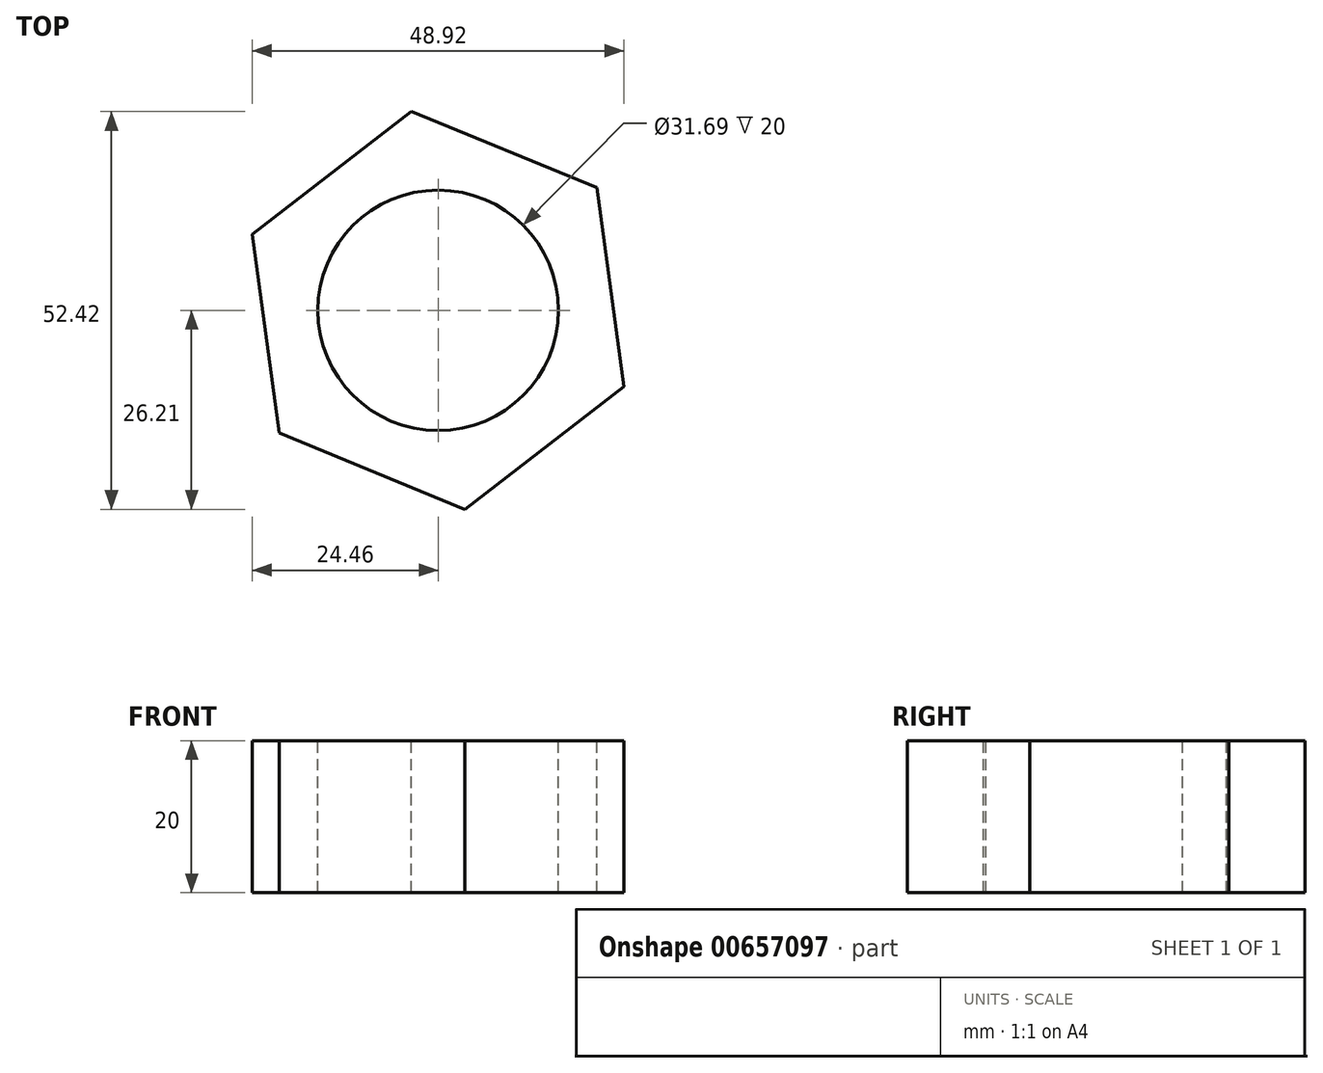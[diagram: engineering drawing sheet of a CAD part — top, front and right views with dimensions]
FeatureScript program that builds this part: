
annotation { "Feature Type Name" : "Feature", "Feature Type Description" : "" }
export const myFeature = defineFeature(function(context is Context, id is Id, definition is map)
    precondition{}
    {
        {
            var Q0;
            Q0=qCreatedBy(makeId("Top.planeOp"),FACE);
            var sketch = newSketch(context, id + "F0", { "sketchPlane" : qUnion([Q0])});
            skCircle(sketch, "E0.cCircle", {"center": v(0, 0) * mm, "radius": 22.9 * mm, "construction": true});
            skLineSegment(sketch, "E0.0", {"start": v(-3.52, 26.21) * mm, "end": v(20.94, 16.16) * mm});
            skLineSegment(sketch, "E0.1", {"start": v(20.94, 16.16) * mm, "end": v(24.46, -10.05) * mm});
            skLineSegment(sketch, "E0.2", {"start": v(24.46, -10.05) * mm, "end": v(3.52, -26.21) * mm});
            skLineSegment(sketch, "E0.3", {"start": v(3.52, -26.21) * mm, "end": v(-20.94, -16.16) * mm});
            skLineSegment(sketch, "E0.4", {"start": v(-20.94, -16.16) * mm, "end": v(-24.46, 10.05) * mm});
            skLineSegment(sketch, "E0.5", {"start": v(-24.46, 10.05) * mm, "end": v(-3.52, 26.21) * mm});
            skPoint(sketch, "E0.0.midPoint", {"position": v(8.7, 21.19) * mm});
            skSolve(sketch);
        }
        {
            var Q0;
            Q0 = qSketchRegion(id + "F0", true);
            extrude(context, id + "F1", {"entities" : qUnion([Q0]), "oppositeDirection" : true, "depth" : 20 * mm, "offsetDistance" : 25.4 * mm});
        }
        {
            var Q0;
            Q0=makeQuery(id+"F1.opExtrude","CAP_FACE",FACE,{"disambiguationData":[OSD([sQuery(id+"F0.wireOp",EDGE,"E0.0"),sQuery(id+"F0.wireOp",EDGE,"E0.1"),sQuery(id+"F0.wireOp",EDGE,"E0.2"),sQuery(id+"F0.wireOp",EDGE,"E0.3"),sQuery(id+"F0.wireOp",EDGE,"E0.4"),sQuery(id+"F0.wireOp",EDGE,"E0.5")])],"isStart":true});
            var sketch = newSketch(context, id + "F2", { "sketchPlane" : qUnion([Q0])});
            skCircle(sketch, "E1", {"center": v(0, 0) * mm, "radius": 15.85 * mm});
            skSolve(sketch);
        }
        {
            var Q0;
            Q0=makeQuery(id+"F2.imprint","IMPRINT",FACE,{"disambiguationData":[TD([[makeQuery(id+"F2.imprint","IMPRINT",EDGE,{"derivedFrom":sQuery(id+"F2.wireOp",EDGE,"E1")}),1.0]])]});
            extrude(context, id + "F3", {"entities" : qUnion([Q0]), "operationType" : NewBodyOperationType.REMOVE, "oppositeDirection" : true, "depth" : 25 * mm, "offsetDistance" : 25 * mm});
        }
    });
